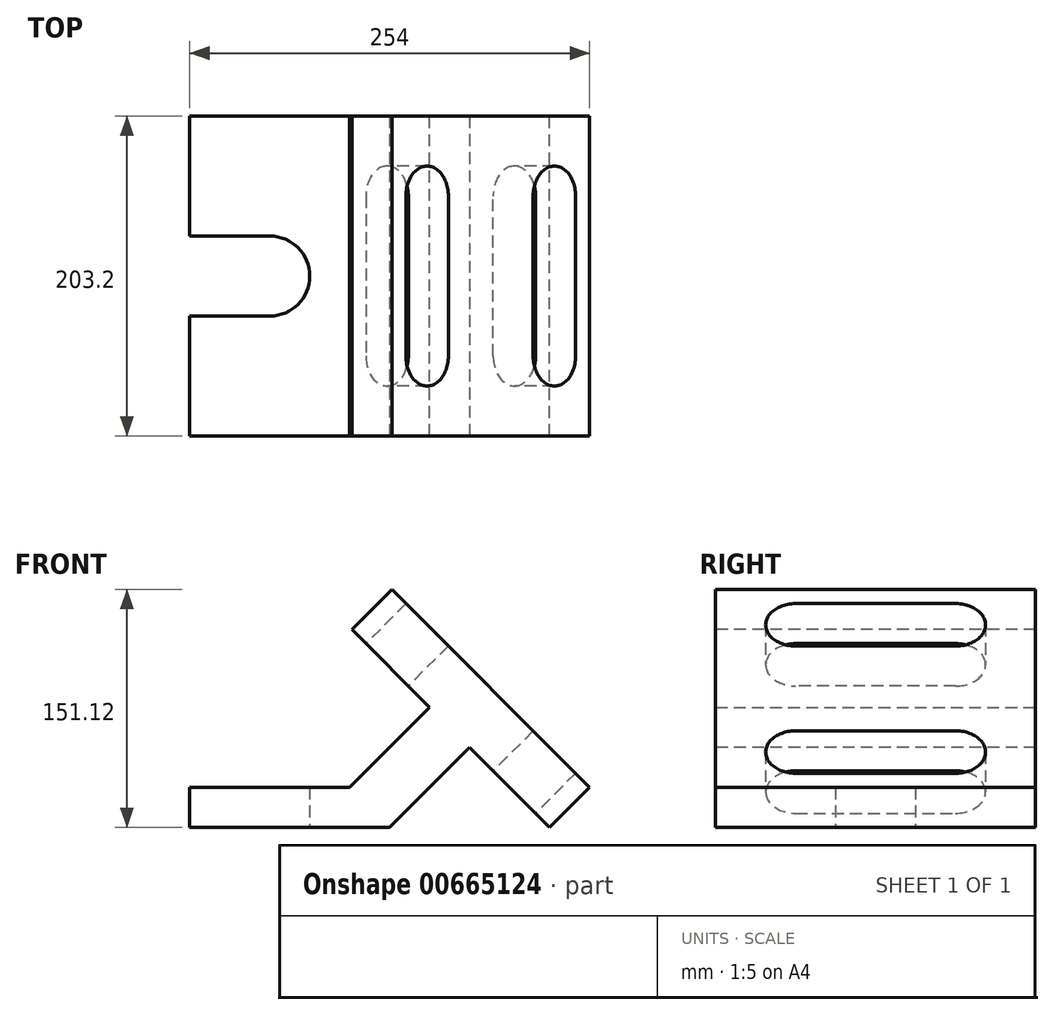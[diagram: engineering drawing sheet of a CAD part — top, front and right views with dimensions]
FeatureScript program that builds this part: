
annotation { "Feature Type Name" : "Feature", "Feature Type Description" : "" }
export const myFeature = defineFeature(function(context is Context, id is Id, definition is map)
    precondition{}
    {
        {
            var Q0;
            Q0=qCreatedBy(makeId("Top.planeOp"),FACE);
            var sketch = newSketch(context, id + "F0", { "sketchPlane" : qUnion([Q0])});
            skLineSegment(sketch, "E0", {"start": v(0, 0) * mm, "end": v(0, 76.2) * mm});
            skLineSegment(sketch, "E1", {"start": v(0, 76.2) * mm, "end": v(50.8, 76.2) * mm});
            skLineSegment(sketch, "E2", {"start": v(50.8, 127) * mm, "end": v(0, 127) * mm});
            skLineSegment(sketch, "E3", {"start": v(0, 127) * mm, "end": v(0, 203.2) * mm});
            skLineSegment(sketch, "E4", {"start": v(0, 203.2) * mm, "end": v(127, 203.2) * mm});
            skLineSegment(sketch, "E5", {"start": v(127, 203.2) * mm, "end": v(127, 0) * mm});
            skLineSegment(sketch, "E6", {"start": v(127, 0) * mm, "end": v(0, 0) * mm});
            skArc(sketch, "E7", {"start": v(50.8, 76.2) * mm, "mid": v(76.2, 101.6) * mm, "end": v(50.8, 127) * mm});
            skSolve(sketch);
        }
        {
            var Q0;
            Q0 = qSketchRegion(id + "F0", true);
            extrude(context, id + "F1", {"entities" : qUnion([Q0]), "depth" : 25.4 * mm, "offsetDistance" : 25.4 * mm});
        }
        {
            var Q0;
            Q0=makeQuery(id+"F1.opExtrude","CAP_EDGE",EDGE,{"disambiguationData":[OSD([sQuery(id+"F0.wireOp",EDGE,"E5")])],"isStart":false});
            chamfer(context, id + "F2", {"entities" : qUnion([Q0]), "chamferType" : ChamferType.OFFSET_ANGLE, "width" : 25.4 * mm, "oppositeDirection" : false, "angle" : 45 * degree, "tangentPropagation" : true});
        }
        {
            var Q0;
            Q0=makeQuery(id+"F2.opChamfer","BLEND_FACE",FACE,{"disambiguationData":[OSD([sQuery(id+"F0.wireOp",EDGE,"E5")])]});
            extrude(context, id + "F3", {"entities" : qUnion([Q0]), "operationType" : NewBodyOperationType.ADD, "depth" : 71.84 * mm, "offsetDistance" : 25.4 * mm});
        }
        {
            var Q0;
            Q0=makeQuery(id+"F3.opExtrude","CAP_FACE",FACE,{"disambiguationData":[OSD([sQuery(id+"F0.wireOp",EDGE,"E5")])],"isStart":false});
            var sketch = newSketch(context, id + "F4", { "sketchPlane" : qUnion([Q0])});
            skLineSegment(sketch, "E8", {"start": v(0, -53.88) * mm, "end": v(0, -89.8) * mm});
            skLineSegment(sketch, "E9", {"start": v(0, -89.8) * mm, "end": v(0, -161.64) * mm});
            skLineSegment(sketch, "E10", {"start": v(0, -161.64) * mm, "end": v(203.2, -161.64) * mm});
            skLineSegment(sketch, "E11", {"start": v(203.2, -161.64) * mm, "end": v(203.2, 16.16) * mm});
            skLineSegment(sketch, "E12", {"start": v(203.2, 16.16) * mm, "end": v(0, 16.16) * mm});
            skLineSegment(sketch, "E13", {"start": v(0, 16.16) * mm, "end": v(0, -89.8) * mm});
            skLineSegment(sketch, "E14", {"start": v(50.8, -129.9) * mm, "end": v(152.4, -129.9) * mm});
            skLineSegment(sketch, "E15", {"start": v(152.4, -15.6) * mm, "end": v(50.8, -15.6) * mm});
            skLineSegment(sketch, "E16.0", {"start": v(152.4, 3.46) * mm, "end": v(50.8, 3.46) * mm});
            skLineSegment(sketch, "E17.0", {"start": v(152.4, -34.64) * mm, "end": v(50.8, -34.64) * mm});
            skLineSegment(sketch, "E18.0", {"start": v(50.8, -148.94) * mm, "end": v(152.4, -148.94) * mm});
            skLineSegment(sketch, "E19.0", {"start": v(50.8, -110.84) * mm, "end": v(152.4, -110.84) * mm});
            skArc(sketch, "E20", {"start": v(50.8, 3.46) * mm, "mid": v(31.75, -15.6) * mm, "end": v(50.8, -34.64) * mm});
            skArc(sketch, "E21", {"start": v(152.4, -34.64) * mm, "mid": v(171.45, -15.6) * mm, "end": v(152.4, 3.46) * mm});
            skArc(sketch, "E22", {"start": v(152.4, -148.94) * mm, "mid": v(171.45, -129.9) * mm, "end": v(152.4, -110.84) * mm});
            skArc(sketch, "E23", {"start": v(50.8, -110.84) * mm, "mid": v(31.75, -129.9) * mm, "end": v(50.8, -148.94) * mm});
            skSolve(sketch);
        }
        {
            var Q0;
            {var subQ10=sQuery(id+"F4.wireOp",EDGE,"E12");Q0=makeQuery(id+"F4.imprint","IMPRINT",FACE,{"disambiguationData":[TD([[makeQuery(id+"F4.imprint","IMPRINT",EDGE,{"derivedFrom":subQ10}),1.0]])]});}
            var Q1;
            {var subQ1=sQuery(id+"F0.wireOp",EDGE,"E7");var subQ2=sQuery(id+"F0.wireOp",EDGE,"E6");var subQ3=sQuery(id+"F0.wireOp",EDGE,"E5");var subQ4=sQuery(id+"F0.wireOp",EDGE,"E4");var subQ5=sQuery(id+"F0.wireOp",EDGE,"E3");var subQ6=sQuery(id+"F0.wireOp",EDGE,"E2");var subQ7=sQuery(id+"F0.wireOp",EDGE,"E1");var subQ8=sQuery(id+"F0.wireOp",EDGE,"E0");var subQ9=makeQuery(id+"F1.opExtrude","CAP_EDGE",EDGE,{"disambiguationData":[OSD([subQ3])],"isStart":false});var subQ10=makeQuery(id+"F3.opExtrude","CAP_EDGE",EDGE,{"disambiguationData":[OSD([subQ8,subQ7,subQ6,subQ5,subQ4,subQ3,subQ2,subQ1]),TDD([makeQuery(id+"F2.opChamfer","BLEND_EDGE",EDGE,{"blendedFrom":[subQ9,makeQuery(id+"F1.opExtrude","CAP_FACE",FACE,{"disambiguationData":[OSD([subQ8,subQ7,subQ6,subQ5,subQ4,subQ3,subQ2,subQ1])],"isStart":true})],"blendedInto":[makeQuery(id+"F1.opExtrude","CAP_FACE",FACE,{"disambiguationData":[OSD([subQ8,subQ7,subQ6,subQ5,subQ4,subQ3,subQ2,subQ1])],"isStart":true})]})])],"isStart":false});Q1=makeQuery(id+"F4.imprint","IMPRINT",FACE,{"disambiguationData":[TD([[makeQuery(id+"F4.imprint","IMPRINT",EDGE,{"derivedFrom":subQ10}),-1.0]])]});}
            var Q2;
            Q2=makeQuery(id+"F4.imprint","IMPRINT",FACE,{"disambiguationData":[TD([[makeQuery(id+"F4.imprint","IMPRINT",EDGE,{"derivedFrom":sQuery(id+"F4.wireOp",EDGE,"E9")}),1.0]])]});
            extrude(context, id + "F5", {"entities" : qUnion([Q0, Q1, Q2]), "operationType" : NewBodyOperationType.ADD, "depth" : 35.92 * mm, "offsetDistance" : 25.4 * mm});
        }
    });
